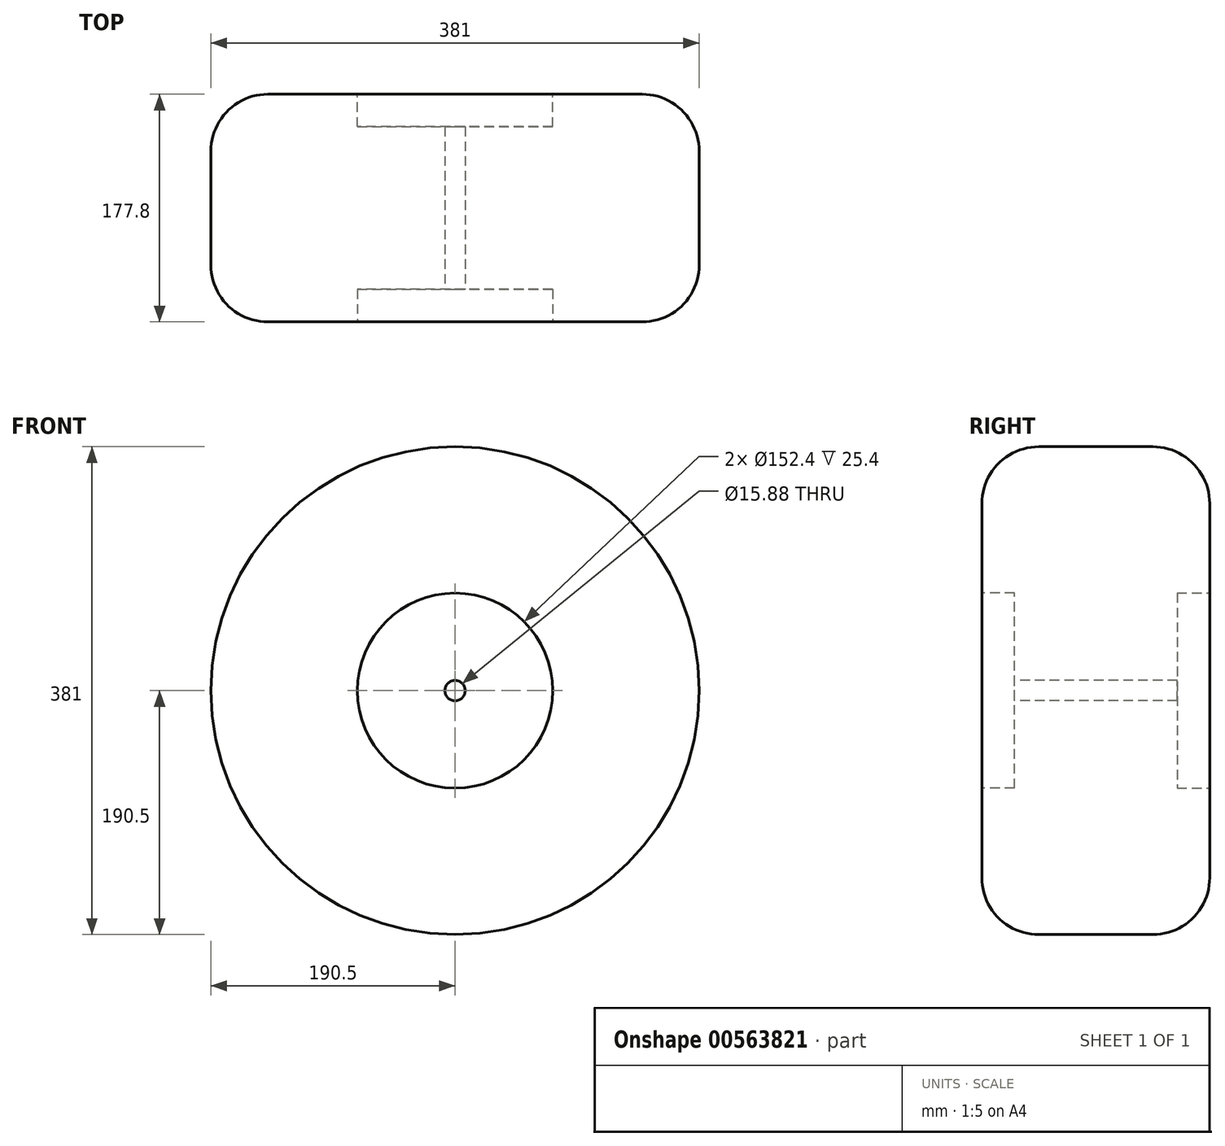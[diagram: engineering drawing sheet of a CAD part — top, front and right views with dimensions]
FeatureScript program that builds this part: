
annotation { "Feature Type Name" : "Feature", "Feature Type Description" : "" }
export const myFeature = defineFeature(function(context is Context, id is Id, definition is map)
    precondition{}
    {
        {
            var Q0;
            Q0=qCreatedBy(makeId("Front.planeOp"),FACE);
            var sketch = newSketch(context, id + "F0", { "sketchPlane" : qUnion([Q0])});
            skCircle(sketch, "E0", {"center": v(0, 0) * mm, "radius": 190.5 * mm});
            skSolve(sketch);
        }
        {
            var Q0;
            Q0=makeQuery(id+"F0.imprint","IMPRINT",FACE,{"disambiguationData":[TD([[makeQuery(id+"F0.imprint","IMPRINT",EDGE,{"derivedFrom":sQuery(id+"F0.wireOp",EDGE,"E0")}),1.0]])]});
            extrude(context, id + "F1", {"entities" : qUnion([Q0]), "endBound" : BoundingType.SYMMETRIC, "depth" : 177.8 * mm, "offsetDistance" : 25.4 * mm});
        }
        {
            var Q0;
            Q0=makeQuery(id+"F1.opExtrude","CAP_FACE",FACE,{"disambiguationData":[OSD([sQuery(id+"F0.wireOp",EDGE,"E0")])],"isStart":false});
            var sketch = newSketch(context, id + "F2", { "sketchPlane" : qUnion([Q0])});
            skCircle(sketch, "E1", {"center": v(0, 0) * mm, "radius": 76.2 * mm});
            skSolve(sketch);
        }
        {
            var Q0;
            Q0=makeQuery(id+"F2.imprint","IMPRINT",FACE,{"disambiguationData":[TD([[makeQuery(id+"F2.imprint","IMPRINT",EDGE,{"derivedFrom":sQuery(id+"F2.wireOp",EDGE,"E1")}),1.0]])]});
            extrude(context, id + "F3", {"entities" : qUnion([Q0]), "operationType" : NewBodyOperationType.REMOVE, "oppositeDirection" : true, "depth" : 25.4 * mm, "offsetDistance" : 25.4 * mm});
        }
        {
            var Q0;
            Q0=makeQuery(id+"F1.opExtrude","CAP_FACE",FACE,{"disambiguationData":[OSD([sQuery(id+"F0.wireOp",EDGE,"E0")])],"isStart":true});
            var sketch = newSketch(context, id + "F4", { "sketchPlane" : qUnion([Q0])});
            skCircle(sketch, "E2", {"center": v(0, 0) * mm, "radius": 76.2 * mm});
            skSolve(sketch);
        }
        {
            var Q0;
            Q0=makeQuery(id+"F4.imprint","IMPRINT",FACE,{"disambiguationData":[TD([[makeQuery(id+"F4.imprint","IMPRINT",EDGE,{"derivedFrom":sQuery(id+"F4.wireOp",EDGE,"E2")}),1.0]])]});
            extrude(context, id + "F5", {"entities" : qUnion([Q0]), "operationType" : NewBodyOperationType.REMOVE, "oppositeDirection" : true, "depth" : 25.4 * mm, "offsetDistance" : 25.4 * mm});
        }
        {
            var Q0;
            Q0=makeQuery(id+"F3.boolean.opBoolean","COPY",FACE,{"derivedFrom":makeQuery(id+"F3.opExtrude","CAP_FACE",FACE,{"disambiguationData":[OSD([sQuery(id+"F2.wireOp",EDGE,"E1")])],"isStart":false})});
            var sketch = newSketch(context, id + "F6", { "sketchPlane" : qUnion([Q0])});
            skCircle(sketch, "E3", {"center": v(0, 0) * mm, "radius": 7.94 * mm});
            skSolve(sketch);
        }
        {
            var Q0;
            Q0=makeQuery(id+"F6.imprint","IMPRINT",FACE,{"disambiguationData":[TD([[makeQuery(id+"F6.imprint","IMPRINT",EDGE,{"derivedFrom":sQuery(id+"F6.wireOp",EDGE,"E3")}),1.0]])]});
            extrude(context, id + "F7", {"entities" : qUnion([Q0]), "operationType" : NewBodyOperationType.REMOVE, "endBound" : BoundingType.SYMMETRIC, "oppositeDirection" : true, "depth" : 254 * mm, "offsetDistance" : 25.4 * mm});
        }
        {
            var Q0;
            Q0=makeQuery(id+"F1.opExtrude","CAP_EDGE",EDGE,{"disambiguationData":[OSD([sQuery(id+"F0.wireOp",EDGE,"E0")])],"isStart":true});
            var Q1;
            Q1=makeQuery(id+"F1.opExtrude","CAP_EDGE",EDGE,{"disambiguationData":[OSD([sQuery(id+"F0.wireOp",EDGE,"E0")])],"isStart":false});
            fillet(context, id + "F8", {"entities" : qUnion([Q0, Q1]), "radius" : 44.45 * mm, "tangentPropagation" : true, "allowEdgeOverflow" : false});
        }
    });
